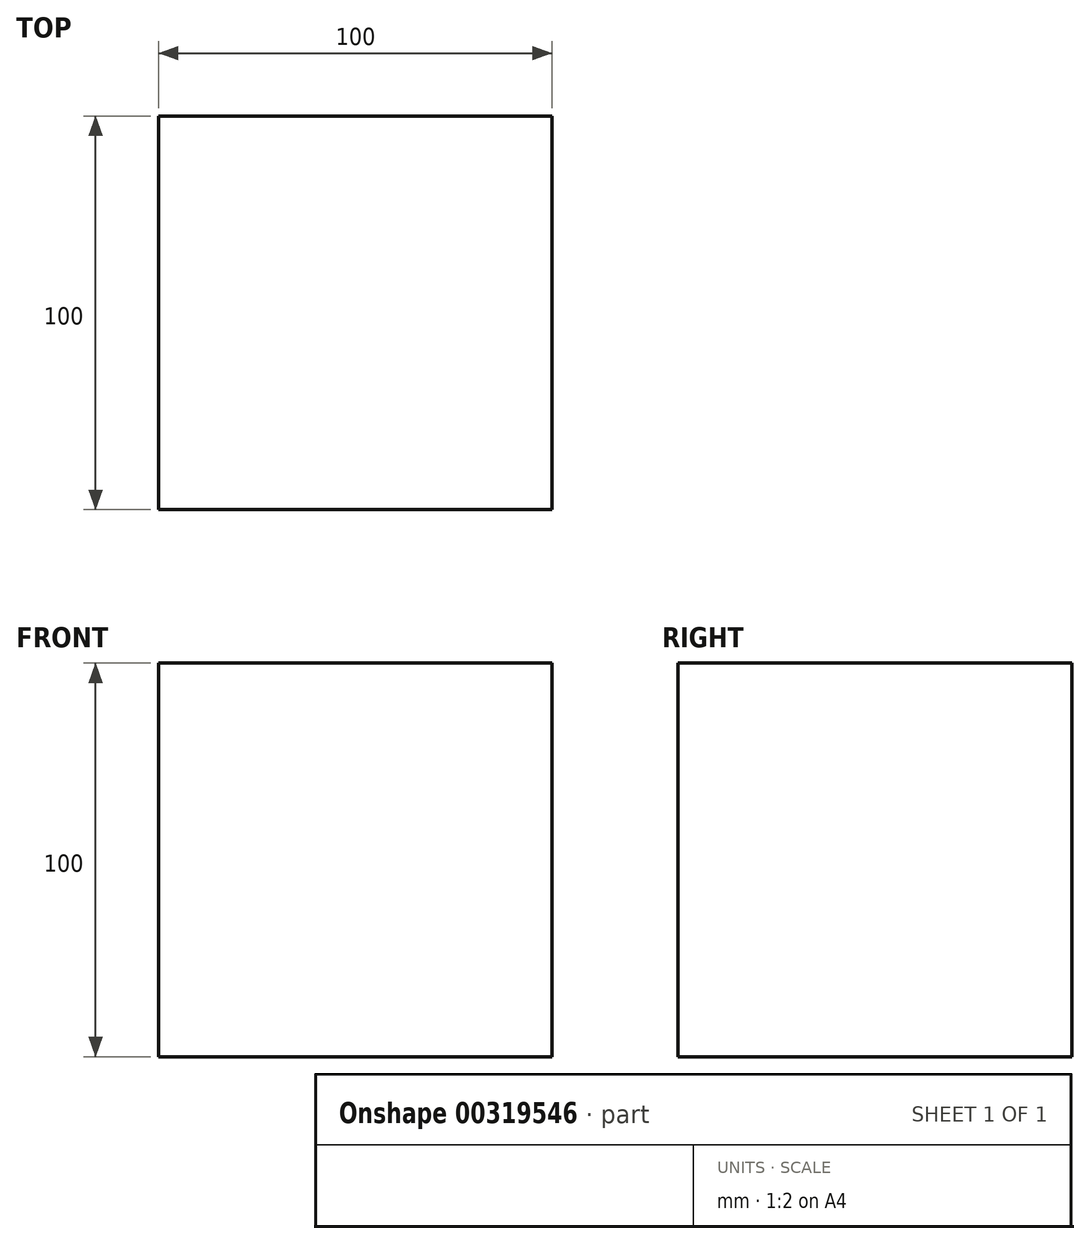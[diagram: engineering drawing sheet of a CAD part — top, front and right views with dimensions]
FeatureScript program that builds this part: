
annotation { "Feature Type Name" : "Feature", "Feature Type Description" : "" }
export const myFeature = defineFeature(function(context is Context, id is Id, definition is map)
    precondition{}
    {
        {
            var Q0;
            Q0=qCreatedBy(makeId("Top.planeOp"), FACE);
            var sketch = newSketch(context, id + "F0", { "sketchPlane" : qUnion([Q0])});
            skLineSegment(sketch, "E0.bottom", {"start": v(0, 0) * mm, "end": v(100, 0) * mm});
            skLineSegment(sketch, "E0.top", {"start": v(0, -100) * mm, "end": v(100, -100) * mm});
            skLineSegment(sketch, "E0.left", {"start": v(0, 0) * mm, "end": v(0, -100) * mm});
            skLineSegment(sketch, "E0.right", {"start": v(100, 0) * mm, "end": v(100, -100) * mm});
            skSolve(sketch);
        }
        {
            var Q0;
            Q0 = qSketchRegion(id + "F0", true);
            extrude(context, id + "F1", {"entities" : qUnion([Q0]), "domain" : OperationDomain.MODEL, "flatOperationType" : FlatOperationType.REMOVE, "depth" : 100 * mm, "offsetDistance" : 25.4 * mm});
        }
    });
